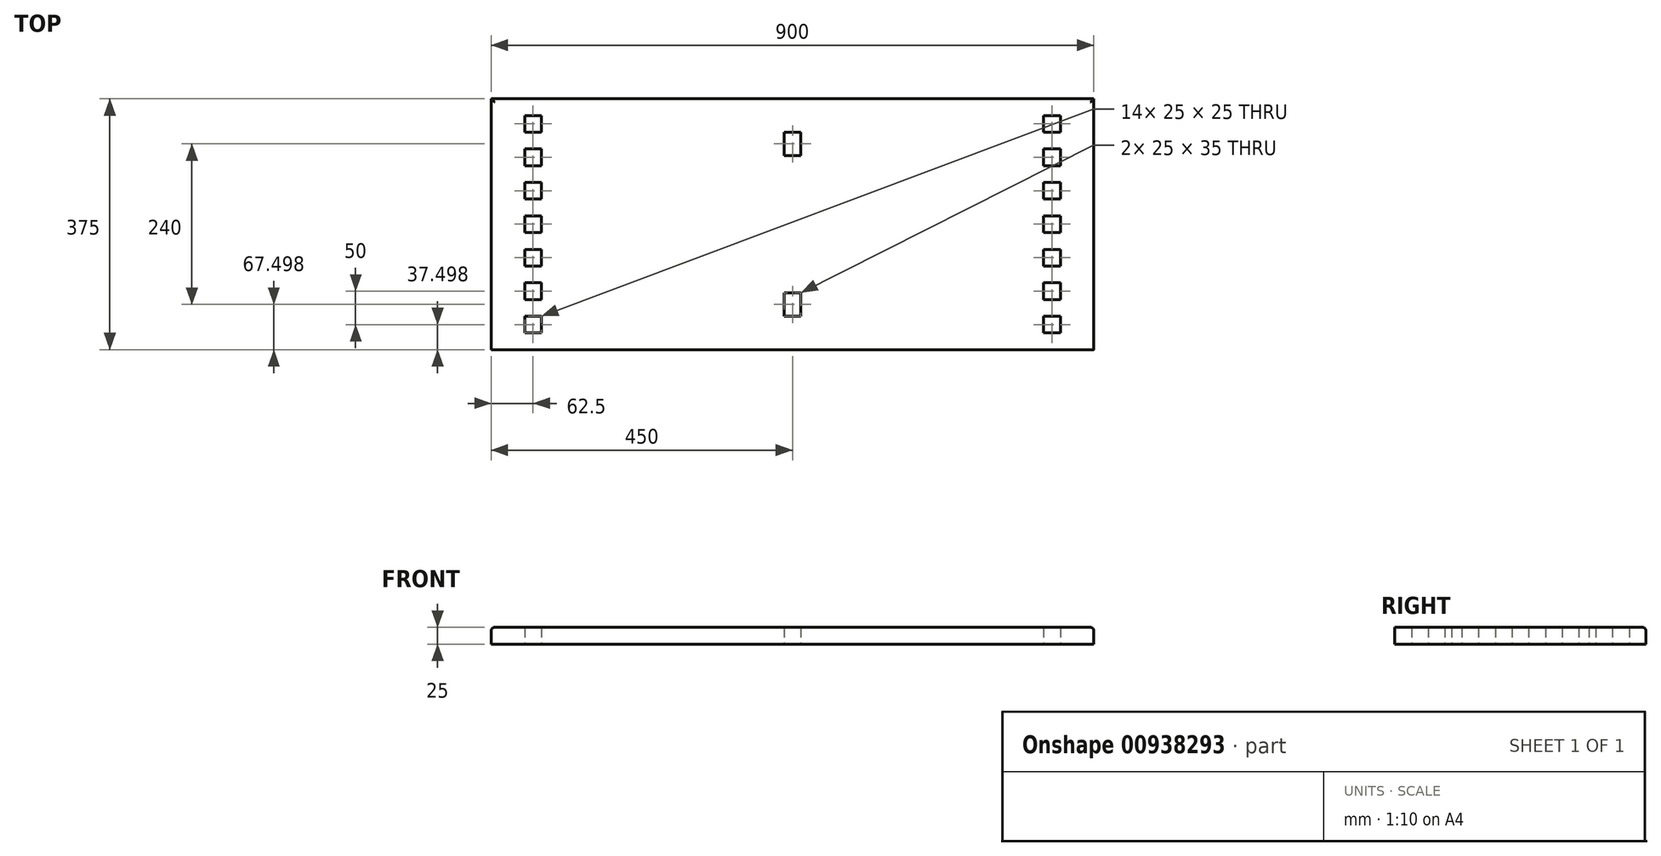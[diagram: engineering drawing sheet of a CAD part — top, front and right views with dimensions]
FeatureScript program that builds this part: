
annotation { "Feature Type Name" : "Feature", "Feature Type Description" : "" }
export const myFeature = defineFeature(function(context is Context, id is Id, definition is map)
    precondition{}
    {
        {
            var Q0;
            Q0=qCreatedBy(makeId("Top.planeOp"),FACE);
            var sketch = newSketch(context, id + "F0", { "sketchPlane" : qUnion([Q0])});
            skLineSegment(sketch, "E0.bottom", {"start": v(-450, 234.06) * mm, "end": v(0, 234.06) * mm});
            skLineSegment(sketch, "E0.top", {"start": v(-450, -140.94) * mm, "end": v(0, -140.94) * mm});
            skLineSegment(sketch, "E0.left", {"start": v(-450, 234.06) * mm, "end": v(-450, -140.94) * mm});
            skLineSegment(sketch, "E0.right", {"start": v(0, 234.06) * mm, "end": v(0, -140.94) * mm});
            skLineSegment(sketch, "E1.bottom", {"start": v(-400, 209.06) * mm, "end": v(-375, 209.06) * mm});
            skLineSegment(sketch, "E1.top", {"start": v(-400, 184.06) * mm, "end": v(-375, 184.06) * mm});
            skLineSegment(sketch, "E1.left", {"start": v(-400, 209.06) * mm, "end": v(-400, 184.06) * mm});
            skLineSegment(sketch, "E1.right", {"start": v(-375, 209.06) * mm, "end": v(-375, 184.06) * mm});
            skLineSegment(sketch, "E2.bottom", {"start": v(-400, 159.06) * mm, "end": v(-375, 159.06) * mm});
            skLineSegment(sketch, "E2.top", {"start": v(-400, 134.06) * mm, "end": v(-375, 134.06) * mm});
            skLineSegment(sketch, "E2.left", {"start": v(-400, 159.06) * mm, "end": v(-400, 134.06) * mm});
            skLineSegment(sketch, "E2.right", {"start": v(-375, 159.06) * mm, "end": v(-375, 134.06) * mm});
            skLineSegment(sketch, "E3.bottom", {"start": v(-400, 109.06) * mm, "end": v(-375, 109.06) * mm});
            skLineSegment(sketch, "E3.top", {"start": v(-400, 84.06) * mm, "end": v(-375, 84.06) * mm});
            skLineSegment(sketch, "E3.left", {"start": v(-400, 109.06) * mm, "end": v(-400, 84.06) * mm});
            skLineSegment(sketch, "E3.right", {"start": v(-375, 109.06) * mm, "end": v(-375, 84.06) * mm});
            skLineSegment(sketch, "E4.bottom", {"start": v(-400, 59.06) * mm, "end": v(-375, 59.06) * mm});
            skLineSegment(sketch, "E4.top", {"start": v(-400, 34.06) * mm, "end": v(-375, 34.06) * mm});
            skLineSegment(sketch, "E4.left", {"start": v(-400, 59.06) * mm, "end": v(-400, 34.06) * mm});
            skLineSegment(sketch, "E4.right", {"start": v(-375, 59.06) * mm, "end": v(-375, 34.06) * mm});
            skLineSegment(sketch, "E5.bottom", {"start": v(-400, 9.06) * mm, "end": v(-375, 9.06) * mm});
            skLineSegment(sketch, "E5.top", {"start": v(-400, -15.94) * mm, "end": v(-375, -15.94) * mm});
            skLineSegment(sketch, "E5.left", {"start": v(-400, 9.06) * mm, "end": v(-400, -15.94) * mm});
            skLineSegment(sketch, "E5.right", {"start": v(-375, 9.06) * mm, "end": v(-375, -15.94) * mm});
            skLineSegment(sketch, "E6.bottom", {"start": v(-400, -40.94) * mm, "end": v(-375, -40.94) * mm});
            skLineSegment(sketch, "E6.top", {"start": v(-400, -65.94) * mm, "end": v(-375, -65.94) * mm});
            skLineSegment(sketch, "E6.left", {"start": v(-400, -40.94) * mm, "end": v(-400, -65.94) * mm});
            skLineSegment(sketch, "E6.right", {"start": v(-375, -40.94) * mm, "end": v(-375, -65.94) * mm});
            skLineSegment(sketch, "E7.bottom", {"start": v(-400, -90.94) * mm, "end": v(-375, -90.94) * mm});
            skLineSegment(sketch, "E7.top", {"start": v(-400, -115.94) * mm, "end": v(-375, -115.94) * mm});
            skLineSegment(sketch, "E7.left", {"start": v(-400, -90.94) * mm, "end": v(-400, -115.94) * mm});
            skLineSegment(sketch, "E7.right", {"start": v(-375, -90.94) * mm, "end": v(-375, -115.94) * mm});
            skSolve(sketch);
        }
        {
            var Q0;
            Q0=makeQuery(id+"F0.imprint","IMPRINT",FACE,{"disambiguationData":[TD([[makeQuery(id+"F0.imprint","IMPRINT",EDGE,{"derivedFrom":sQuery(id+"F0.wireOp",EDGE,"E0.bottom")}),-1.0]])]});
            extrude(context, id + "F1", {"entities" : qUnion([Q0]), "depth" : 25 * mm, "offsetDistance" : 25 * mm});
        }
        {
            var Q0;
            Q0=makeQuery(id+"F1.opExtrude","SWEPT_BODY",BODY,{"disambiguationData":[OSD([sQuery(id+"F0.wireOp",EDGE,"E0.bottom"),sQuery(id+"F0.wireOp",EDGE,"E0.top"),sQuery(id+"F0.wireOp",EDGE,"E0.left"),sQuery(id+"F0.wireOp",EDGE,"E0.right"),sQuery(id+"F0.wireOp",EDGE,"E1.bottom"),sQuery(id+"F0.wireOp",EDGE,"E1.top"),sQuery(id+"F0.wireOp",EDGE,"E1.left"),sQuery(id+"F0.wireOp",EDGE,"E1.right"),sQuery(id+"F0.wireOp",EDGE,"E2.bottom"),sQuery(id+"F0.wireOp",EDGE,"E2.top"),sQuery(id+"F0.wireOp",EDGE,"E2.left"),sQuery(id+"F0.wireOp",EDGE,"E2.right"),sQuery(id+"F0.wireOp",EDGE,"E3.bottom"),sQuery(id+"F0.wireOp",EDGE,"E3.top"),sQuery(id+"F0.wireOp",EDGE,"E3.left"),sQuery(id+"F0.wireOp",EDGE,"E3.right"),sQuery(id+"F0.wireOp",EDGE,"E4.bottom"),sQuery(id+"F0.wireOp",EDGE,"E4.top"),sQuery(id+"F0.wireOp",EDGE,"E4.left"),sQuery(id+"F0.wireOp",EDGE,"E4.right"),sQuery(id+"F0.wireOp",EDGE,"E5.bottom"),sQuery(id+"F0.wireOp",EDGE,"E5.top"),sQuery(id+"F0.wireOp",EDGE,"E5.left"),sQuery(id+"F0.wireOp",EDGE,"E5.right"),sQuery(id+"F0.wireOp",EDGE,"E6.bottom"),sQuery(id+"F0.wireOp",EDGE,"E6.top"),sQuery(id+"F0.wireOp",EDGE,"E6.left"),sQuery(id+"F0.wireOp",EDGE,"E6.right"),sQuery(id+"F0.wireOp",EDGE,"E7.bottom"),sQuery(id+"F0.wireOp",EDGE,"E7.top"),sQuery(id+"F0.wireOp",EDGE,"E7.left"),sQuery(id+"F0.wireOp",EDGE,"E7.right")])]});
            var Q1;
            Q1=makeQuery(id+"F1.opExtrude","SWEPT_FACE",FACE,{"disambiguationData":[OSD([sQuery(id+"F0.wireOp",EDGE,"E0.right")])]});
            mirror(context, id + "F2", {"operationType" : NewBodyOperationType.ADD, "entities" : qUnion([Q0]), "mirrorPlane" : qUnion([Q1])});
        }
        {
            var Q0;
            {var subQ0=makeQuery(id+"F1.opExtrude","CAP_FACE",FACE,{"disambiguationData":[OSD([sQuery(id+"F0.wireOp",EDGE,"E0.bottom"),sQuery(id+"F0.wireOp",EDGE,"E0.top"),sQuery(id+"F0.wireOp",EDGE,"E0.left"),sQuery(id+"F0.wireOp",EDGE,"E0.right"),sQuery(id+"F0.wireOp",EDGE,"E1.bottom"),sQuery(id+"F0.wireOp",EDGE,"E1.top"),sQuery(id+"F0.wireOp",EDGE,"E1.left"),sQuery(id+"F0.wireOp",EDGE,"E1.right"),sQuery(id+"F0.wireOp",EDGE,"E2.bottom"),sQuery(id+"F0.wireOp",EDGE,"E2.top"),sQuery(id+"F0.wireOp",EDGE,"E2.left"),sQuery(id+"F0.wireOp",EDGE,"E2.right"),sQuery(id+"F0.wireOp",EDGE,"E3.bottom"),sQuery(id+"F0.wireOp",EDGE,"E3.top"),sQuery(id+"F0.wireOp",EDGE,"E3.left"),sQuery(id+"F0.wireOp",EDGE,"E3.right"),sQuery(id+"F0.wireOp",EDGE,"E4.bottom"),sQuery(id+"F0.wireOp",EDGE,"E4.top"),sQuery(id+"F0.wireOp",EDGE,"E4.left"),sQuery(id+"F0.wireOp",EDGE,"E4.right"),sQuery(id+"F0.wireOp",EDGE,"E5.bottom"),sQuery(id+"F0.wireOp",EDGE,"E5.top"),sQuery(id+"F0.wireOp",EDGE,"E5.left"),sQuery(id+"F0.wireOp",EDGE,"E5.right"),sQuery(id+"F0.wireOp",EDGE,"E6.bottom"),sQuery(id+"F0.wireOp",EDGE,"E6.top"),sQuery(id+"F0.wireOp",EDGE,"E6.left"),sQuery(id+"F0.wireOp",EDGE,"E6.right"),sQuery(id+"F0.wireOp",EDGE,"E7.bottom"),sQuery(id+"F0.wireOp",EDGE,"E7.top"),sQuery(id+"F0.wireOp",EDGE,"E7.left"),sQuery(id+"F0.wireOp",EDGE,"E7.right")])],"isStart":true});Q0=makeQuery(id+"F2.boolean.opBoolean","MERGE",FACE,{"derivedFrom":[subQ0,makeQuery(id+"F2.opPattern","COPY",FACE,{"derivedFrom":subQ0,"instanceName":"1"})]});}
            var sketch = newSketch(context, id + "F3", { "sketchPlane" : qUnion([Q0])});
            skLineSegment(sketch, "E8.bottom", {"start": v(12.5, 55.94) * mm, "end": v(-12.5, 55.94) * mm});
            skLineSegment(sketch, "E8.top", {"start": v(12.5, 90.94) * mm, "end": v(-12.5, 90.94) * mm});
            skLineSegment(sketch, "E8.left", {"start": v(12.5, 55.94) * mm, "end": v(12.5, 90.94) * mm});
            skLineSegment(sketch, "E8.right", {"start": v(-12.5, 55.94) * mm, "end": v(-12.5, 90.94) * mm});
            skLineSegment(sketch, "E9.bottom", {"start": v(12.5, -184.06) * mm, "end": v(-12.5, -184.06) * mm});
            skLineSegment(sketch, "E9.top", {"start": v(12.5, -149.06) * mm, "end": v(-12.5, -149.06) * mm});
            skLineSegment(sketch, "E9.left", {"start": v(12.5, -184.06) * mm, "end": v(12.5, -149.06) * mm});
            skLineSegment(sketch, "E9.right", {"start": v(-12.5, -184.06) * mm, "end": v(-12.5, -149.06) * mm});
            skSolve(sketch);
        }
        {
            var Q0;
            Q0=makeQuery(id+"F3.imprint","IMPRINT",FACE,{"disambiguationData":[TD([[makeQuery(id+"F3.imprint","IMPRINT",EDGE,{"derivedFrom":sQuery(id+"F3.wireOp",EDGE,"E9.bottom")}),-1.0]])]});
            var Q1;
            Q1=makeQuery(id+"F3.imprint","IMPRINT",FACE,{"disambiguationData":[TD([[makeQuery(id+"F3.imprint","IMPRINT",EDGE,{"derivedFrom":sQuery(id+"F3.wireOp",EDGE,"E8.bottom")}),-1.0]])]});
            extrude(context, id + "F4", {"entities" : qUnion([Q0, Q1]), "operationType" : NewBodyOperationType.REMOVE, "oppositeDirection" : true, "depth" : 25 * mm, "offsetDistance" : 25 * mm});
        }
        {
            var Q0;
            {var subQ0=makeQuery(id+"F1.opExtrude","CAP_EDGE",EDGE,{"disambiguationData":[OSD([sQuery(id+"F0.wireOp",EDGE,"E0.bottom")])],"isStart":false});Q0=makeQuery(id+"F2.boolean.opBoolean","MERGE",EDGE,{"derivedFrom":[subQ0,makeQuery(id+"F2.opPattern","COPY",EDGE,{"derivedFrom":subQ0,"instanceName":"1"})]});}
            var Q1;
            Q1=makeQuery(id+"F2.opPattern","COPY",EDGE,{"derivedFrom":makeQuery(id+"F1.opExtrude","CAP_EDGE",EDGE,{"disambiguationData":[OSD([sQuery(id+"F0.wireOp",EDGE,"E0.left")])],"isStart":false}),"instanceName":"1"});
            var Q2;
            Q2=makeQuery(id+"F1.opExtrude","CAP_EDGE",EDGE,{"disambiguationData":[OSD([sQuery(id+"F0.wireOp",EDGE,"E0.left")])],"isStart":false});
            fillet(context, id + "F5", {"entities" : qUnion([Q0, Q1, Q2]), "radius" : 5 * mm, "tangentPropagation" : true, "allowEdgeOverflow" : false});
        }
    });
